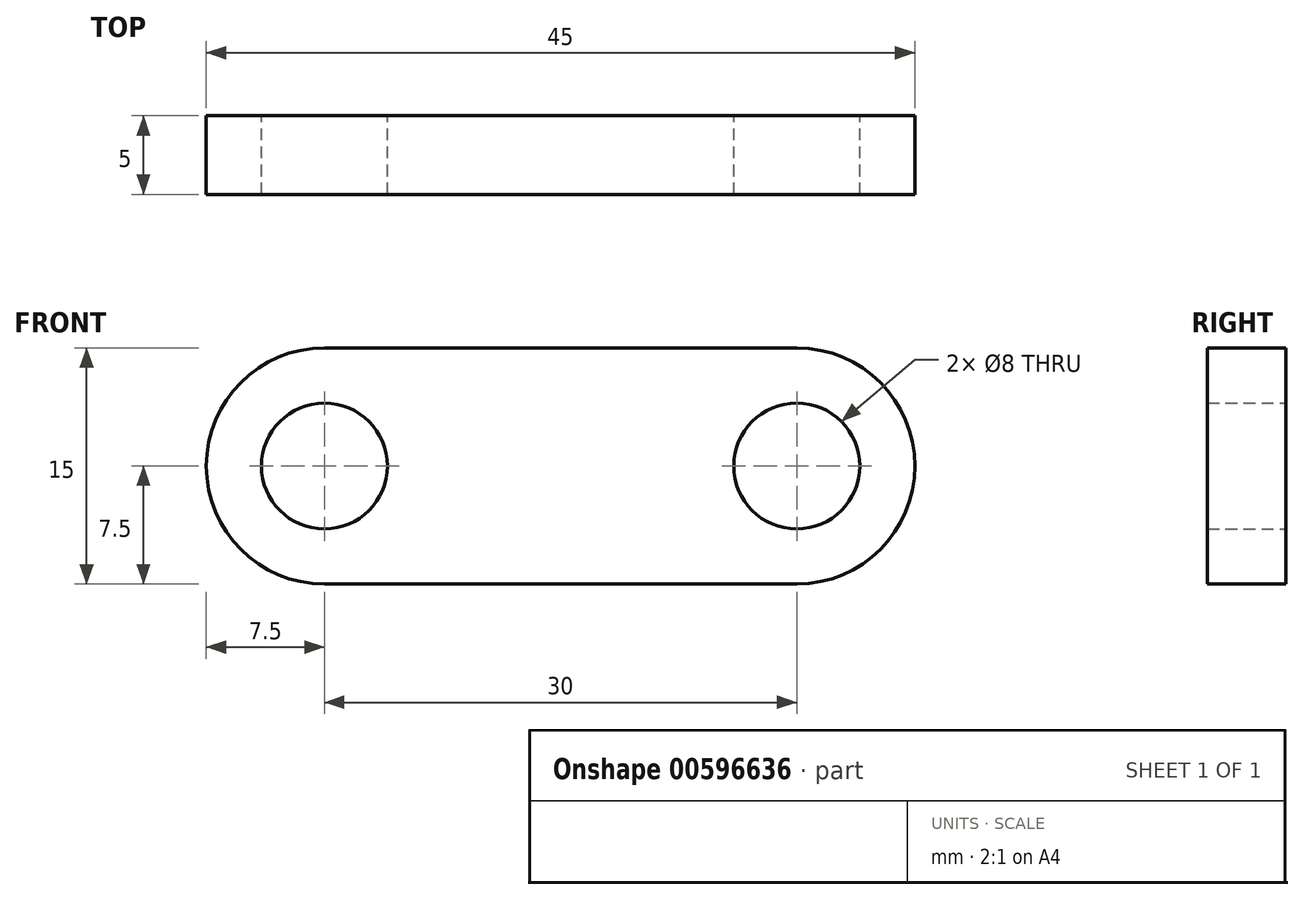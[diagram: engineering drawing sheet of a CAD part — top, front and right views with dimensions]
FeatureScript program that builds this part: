
annotation { "Feature Type Name" : "Feature", "Feature Type Description" : "" }
export const myFeature = defineFeature(function(context is Context, id is Id, definition is map)
    precondition{}
    {
        {
            var Q0;
            Q0=qCreatedBy(makeId("Front.planeOp"),FACE);
            var sketch = newSketch(context, id + "F0", { "sketchPlane" : qUnion([Q0])});
            skArc(sketch, "E0", {"start": v(0, 7.5) * mm, "mid": v(-7.5, 0) * mm, "end": v(0, -7.5) * mm});
            skCircle(sketch, "E1", {"center": v(0, 0) * mm, "radius": 4 * mm});
            skArc(sketch, "E2", {"start": v(30, -7.5) * mm, "mid": v(37.5, 0) * mm, "end": v(30, 7.5) * mm});
            skCircle(sketch, "E3", {"center": v(30, 0) * mm, "radius": 4 * mm});
            skLineSegment(sketch, "E4", {"start": v(0, 7.5) * mm, "end": v(30, 7.5) * mm});
            skLineSegment(sketch, "E5", {"start": v(0, -7.5) * mm, "end": v(30, -7.5) * mm});
            skSolve(sketch);
        }
        {
            var Q0;
            Q0 = qSketchRegion(id + "F0", true);
            extrude(context, id + "F1", {"entities" : qUnion([Q0]), "depth" : 5 * mm, "offsetDistance" : 25 * mm});
        }
    });
